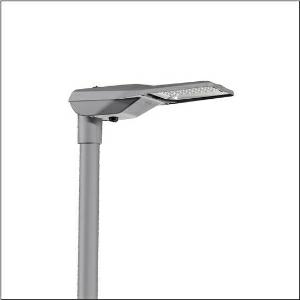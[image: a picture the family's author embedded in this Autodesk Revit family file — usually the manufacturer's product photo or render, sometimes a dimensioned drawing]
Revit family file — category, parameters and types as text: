
# Revit family: streetlight_sl_21_iq_mini___st1_0ab_5xe2m31y08hb_576a
name_source: partatom
category: Lighting Fixtures
units: mm (PartAtom-declared; Revit-internal decimal feet)

## family parameters
Cut with Voids When Loaded = No
Host = Face
Light Source = No
Part Type = Normal
Room Calculation Point = No
Round Connector Dimension = Use Diameter
Shared = No

## types (1)
- --- (1 x LED, 8580 lm, 71 W, 3000K)
    Apparent Load = 71 VA
    CIE Flux Codes = 38 73 97 100 100
    Color Rendering = 70
    Color Temperature = 3000K
    Default Elevation = 1800 mm
    Description = Streetlight SL 21 iQ mini, mast luminaire, primary light control with lens, of PMMA, primary optical cover: cover, of toughened safety glass, transparent, light distribution: ST1.0aB, light emission: direct distribution, primary light characteristic: asymmetric, installation type: post-top, side-entry, LED, High Power LED, rated luminous flux: 8.580lm, luminous efficacy: 121lm/W, light colour: 730, colour temperature: 3000K, control gear: iQ-Street Remote, D4i with power reduction, control: pre-setting: logarithmic dimming characteristic, Street-Remote, Auto-Match, Temp-Guard, Lumen-Switch, Night-Set, Smart-Wire, Light-Fading, Desk-Remote (wireless, voltage-free reading and setting of iQ features in the workshop via application-optimized NFC function/RFID function), optimised constant luminous flux control (CLO 2.0), mains connection: 220..240V, AC, 50/60Hz, start of lifetime: 71W, end of service life: 75W, reduction: 30W, luminaire housing, of diecast aluminium, powder-coated, SITECO metallic grey (DB 702S), corrosivity category C5 high according to DIN EN ISO 12944, please order mast flange separately, inclination adjustable: 0°, 5°, 10°, 15°, sealing non-destructively replaceable, multi-level sealing system, length: 628mm, width: 235mm, height: 110mm, mast flange for spigot size: 42mm (side-entry): 5XC10008XM4, 60/48mm (side-entry/post-top): 5XC10108XM2, 76/60mm (side-entry/post-top): 5XC10108XM1, mounting height: 4..8m, Smart Interface below and above, protection rating (complete): IP66, insulation class (complete): insulation class II (safety insulation), certification: CE, ENEC, ENEC+, VDE, impact resistance: IK10, permissible operating ambient temperature for outdoor applications: -40..+50°C, standard-compliant lighting for roads and squares, packaging unit: 1 piece

Light Distribution: ST1.0aB
    Height = 110 mm
    Lamp = 1 x LED
    Lamp Light Flux = 8580 lm
    Lamp Power = 71 W
    Lamp count = 1
    Length = 625 mm
    Luminous efficacy = 121 lm/W
    Manufacturer = Siteco
    ModVariant = No
    Model = 5XE2M31Y08HB
    Number of Poles = 1
    OnlyDefault = Yes
    Power Factor = 1
    Product Name = Streetlight SL 21 iQ mini | ST1.0aB
    Product group = mast luminaire | pylon top
    ProductGroupID = 6100
    Protection Class = Protection class II
    Protection Degree = IP 66
    RLX_Detail_Level = 1
    RLX_Emergency_Light_Flux = 0 lm
    RLX_Emergency_Type = 0
    RLX_Emergency_Type_DB = No
    RlxData = <blob elided: 92817 chars, md5=5404d497>
    Socket = socket
    Standby Power = 0 W
    System Light Flux = 8580 lm
    System Power = 71 W
    Type Comments = factory setting: luminous flux: 100 % | dim-lin: 254 | 716 mA
    Type Image = l_1003514.jpg
    URL = http://relux.com
    VarID = @adj_112391
    Voltage = 0 V
    Weight = 0.00 kg
    Width = 234 mm

## geometry (parser evidence)
native form markers: Blend x4, Sweep x11
no freeform markers — native parametric forms only
